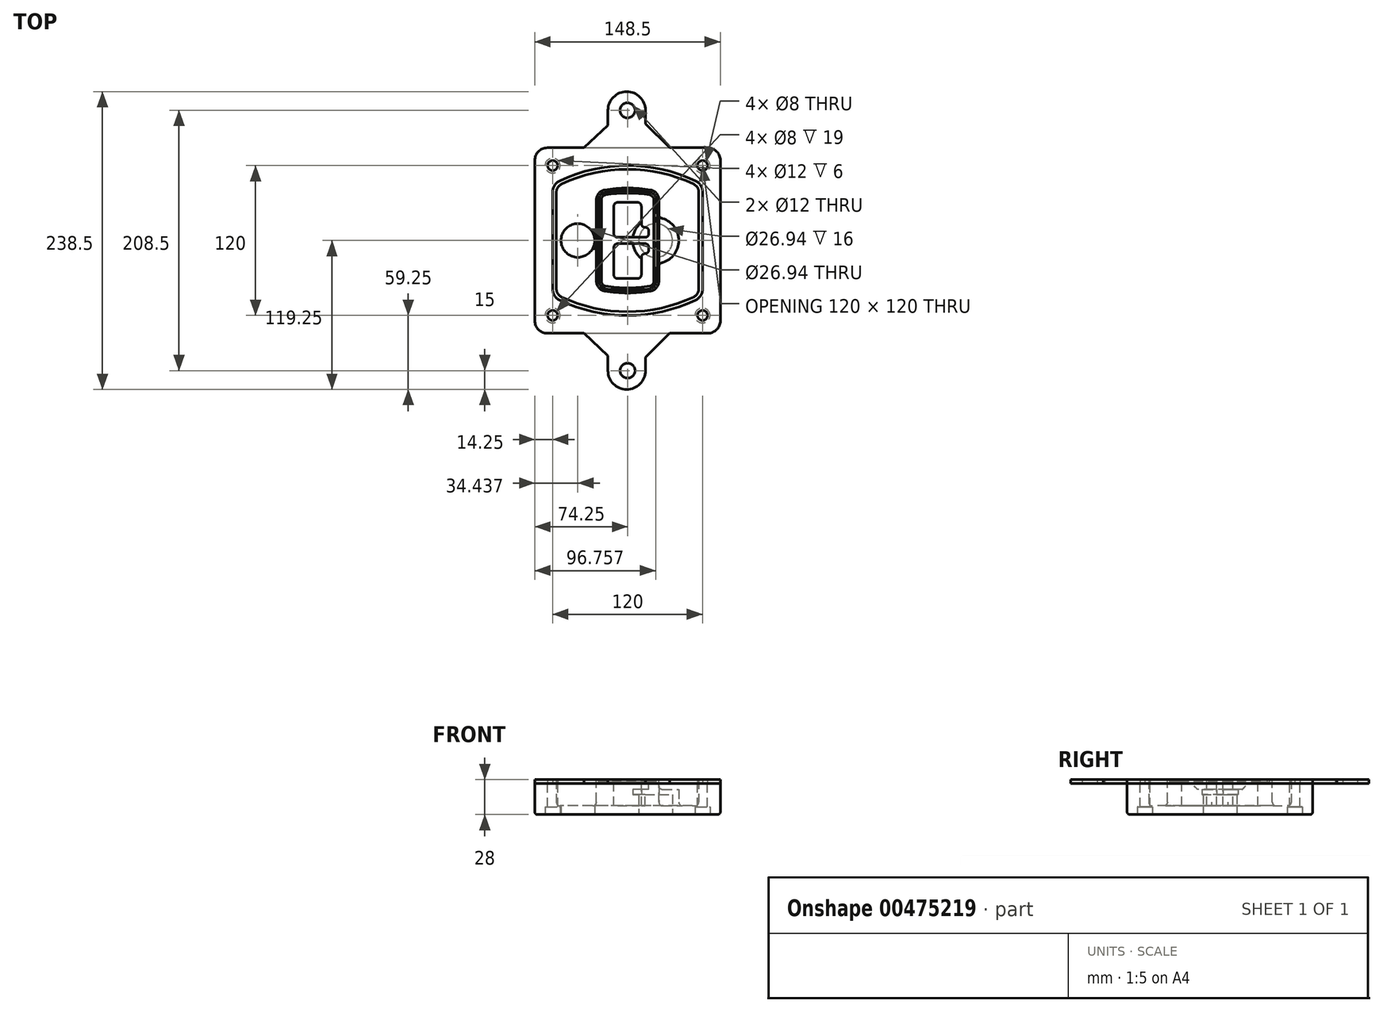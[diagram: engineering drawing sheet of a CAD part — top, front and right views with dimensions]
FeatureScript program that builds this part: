
annotation { "Feature Type Name" : "Feature", "Feature Type Description" : "" }
export const myFeature = defineFeature(function(context is Context, id is Id, definition is map)
    precondition{}
    {
        {
            var Q0;
            Q0=qCreatedBy(makeId("Top.planeOp"),FACE);
            var sketch = newSketch(context, id + "F0", { "sketchPlane" : qUnion([Q0])});
            skPoint(sketch, "E0.rect.middle", {"position": v(0, 0) * mm});
            skLineSegment(sketch, "E1.bottom", {"start": v(-64.25, -74.25) * mm, "end": v(64.25, -74.25) * mm});
            skLineSegment(sketch, "E1.top", {"start": v(-64.25, 74.25) * mm, "end": v(64.25, 74.25) * mm});
            skLineSegment(sketch, "E1.left", {"start": v(-74.25, -64.25) * mm, "end": v(-74.25, 64.25) * mm});
            skLineSegment(sketch, "E1.right", {"start": v(74.25, -64.25) * mm, "end": v(74.25, 64.25) * mm});
            skLineSegment(sketch, "E2", {"start": v(-74.25, 74.25) * mm, "end": v(74.25, -74.25) * mm, "construction": true});
            skLineSegment(sketch, "E3", {"start": v(74.25, 74.25) * mm, "end": v(-74.25, -74.25) * mm, "construction": true});
            skCircle(sketch, "E4", {"center": v(-60, 60) * mm, "radius": 4 * mm});
            skCircle(sketch, "E5", {"center": v(60, 60) * mm, "radius": 4 * mm});
            skCircle(sketch, "E6", {"center": v(60, -60) * mm, "radius": 4 * mm});
            skCircle(sketch, "E7", {"center": v(-60, -60) * mm, "radius": 4 * mm});
            skLineSegment(sketch, "E8", {"start": v(-60, 60) * mm, "end": v(60, 60) * mm, "construction": true});
            skLineSegment(sketch, "E9", {"start": v(60, 60) * mm, "end": v(60, -60) * mm, "construction": true});
            skLineSegment(sketch, "E10", {"start": v(60, -60) * mm, "end": v(-60, -60) * mm, "construction": true});
            skLineSegment(sketch, "E11", {"start": v(-60, -60) * mm, "end": v(-60, 60) * mm, "construction": true});
            skLineSegment(sketch, "E12", {"start": v(-60, 38.83) * mm, "end": v(-60, -38.83) * mm});
            skLineSegment(sketch, "E13", {"start": v(60, 38.83) * mm, "end": v(60, -38.83) * mm});
            skArc(sketch, "E14", {"start": v(54.26, 47.88) * mm, "mid": v(0, 60) * mm, "end": v(-54.26, 47.88) * mm});
            skArc(sketch, "E15", {"start": v(-54.26, -47.88) * mm, "mid": v(0, -60) * mm, "end": v(54.26, -47.88) * mm});
            skLineSegment(sketch, "E16", {"start": v(-60, 0) * mm, "end": v(60, 0) * mm, "construction": true});
            skPoint(sketch, "E17.visualSharp", {"position": v(-60, -45) * mm});
            skArc(sketch, "E17.filletArc", {"start": v(-60, -38.83) * mm, "mid": v(-58.44, -44.2) * mm, "end": v(-54.26, -47.88) * mm});
            skPoint(sketch, "E18.visualSharp", {"position": v(-60, 45) * mm});
            skArc(sketch, "E18.filletArc", {"start": v(-54.26, 47.88) * mm, "mid": v(-58.44, 44.2) * mm, "end": v(-60, 38.83) * mm});
            skPoint(sketch, "E19.visualSharp", {"position": v(60, 45) * mm});
            skArc(sketch, "E19.filletArc", {"start": v(60, 38.83) * mm, "mid": v(58.44, 44.2) * mm, "end": v(54.26, 47.88) * mm});
            skPoint(sketch, "E20.visualSharp", {"position": v(60, -45) * mm});
            skArc(sketch, "E20.filletArc", {"start": v(54.26, -47.88) * mm, "mid": v(58.44, -44.2) * mm, "end": v(60, -38.83) * mm});
            skPoint(sketch, "E21.visualSharp", {"position": v(-74.25, 74.25) * mm});
            skArc(sketch, "E21.filletArc", {"start": v(-64.25, 74.25) * mm, "mid": v(-71.32, 71.32) * mm, "end": v(-74.25, 64.25) * mm});
            skPoint(sketch, "E22.visualSharp", {"position": v(74.25, 74.25) * mm});
            skArc(sketch, "E22.filletArc", {"start": v(74.25, 64.25) * mm, "mid": v(71.32, 71.32) * mm, "end": v(64.25, 74.25) * mm});
            skPoint(sketch, "E23.visualSharp", {"position": v(74.25, -74.25) * mm});
            skArc(sketch, "E23.filletArc", {"start": v(64.25, -74.25) * mm, "mid": v(71.32, -71.32) * mm, "end": v(74.25, -64.25) * mm});
            skPoint(sketch, "E24.visualSharp", {"position": v(-74.25, -74.25) * mm});
            skArc(sketch, "E24.filletArc", {"start": v(-74.25, -64.25) * mm, "mid": v(-71.32, -71.32) * mm, "end": v(-64.25, -74.25) * mm});
            skArc(sketch, "E25.0", {"start": v(57, 38.83) * mm, "mid": v(55.9, 42.58) * mm, "end": v(52.98, 45.17) * mm});
            skLineSegment(sketch, "E25.1", {"start": v(57, 38.83) * mm, "end": v(57, -38.83) * mm});
            skArc(sketch, "E25.2", {"start": v(52.98, -45.17) * mm, "mid": v(55.9, -42.58) * mm, "end": v(57, -38.83) * mm});
            skArc(sketch, "E25.3", {"start": v(-52.98, -45.17) * mm, "mid": v(0, -57) * mm, "end": v(52.98, -45.17) * mm});
            skArc(sketch, "E25.4", {"start": v(-57, -38.83) * mm, "mid": v(-55.9, -42.58) * mm, "end": v(-52.98, -45.17) * mm});
            skArc(sketch, "E25.5", {"start": v(52.98, 45.17) * mm, "mid": v(0, 57) * mm, "end": v(-52.98, 45.17) * mm});
            skLineSegment(sketch, "E25.6", {"start": v(-57, 38.83) * mm, "end": v(-57, -38.83) * mm});
            skArc(sketch, "E25.7", {"start": v(-52.98, 45.17) * mm, "mid": v(-55.9, 42.58) * mm, "end": v(-57, 38.83) * mm});
            skArc(sketch, "E26.0", {"start": v(-55.96, 51.5) * mm, "mid": v(-61.82, 46.33) * mm, "end": v(-64, 38.83) * mm});
            skArc(sketch, "E26.1", {"start": v(55.96, 51.5) * mm, "mid": v(0, 64) * mm, "end": v(-55.96, 51.5) * mm});
            skArc(sketch, "E26.2", {"start": v(64, 38.83) * mm, "mid": v(61.82, 46.33) * mm, "end": v(55.96, 51.5) * mm});
            skLineSegment(sketch, "E26.3", {"start": v(64, 38.83) * mm, "end": v(64, -38.83) * mm});
            skArc(sketch, "E26.4", {"start": v(55.96, -51.5) * mm, "mid": v(61.82, -46.33) * mm, "end": v(64, -38.83) * mm});
            skLineSegment(sketch, "E26.5", {"start": v(-64, 38.83) * mm, "end": v(-64, -38.83) * mm});
            skArc(sketch, "E26.6", {"start": v(-55.96, -51.5) * mm, "mid": v(0, -64) * mm, "end": v(55.96, -51.5) * mm});
            skArc(sketch, "E26.7", {"start": v(-64, -38.83) * mm, "mid": v(-61.82, -46.33) * mm, "end": v(-55.96, -51.5) * mm});
            skSolve(sketch);
        }
        {
            var Q0;
            Q0=makeQuery(id+"F0.imprint","IMPRINT",FACE,{"disambiguationData":[TD([[makeQuery(id+"F0.imprint","IMPRINT",EDGE,{"derivedFrom":sQuery(id+"F0.wireOp",EDGE,"E1.bottom")}),1.0]])]});
            var Q1;
            Q1=makeQuery(id+"F0.imprint","IMPRINT",FACE,{"disambiguationData":[TD([[makeQuery(id+"F0.imprint","IMPRINT",EDGE,{"derivedFrom":sQuery(id+"F0.wireOp",EDGE,"E12")}),1.0]])]});
            var Q2;
            Q2=makeQuery(id+"F0.imprint","IMPRINT",FACE,{"disambiguationData":[TD([[makeQuery(id+"F0.imprint","IMPRINT",EDGE,{"derivedFrom":sQuery(id+"F0.wireOp",EDGE,"E25.0")}),1.0]])]});
            var Q3;
            Q3=makeQuery(id+"F0.imprint","IMPRINT",FACE,{"disambiguationData":[TD([[makeQuery(id+"F0.imprint","IMPRINT",EDGE,{"derivedFrom":sQuery(id+"F0.wireOp",EDGE,"E12")}),-1.0]])]});
            extrude(context, id + "F1", {"entities" : qUnion([Q0, Q1, Q2, Q3]), "oppositeDirection" : true, "depth" : 25 * mm});
        }
        {
            var Q0;
            Q0=makeQuery(id+"F0.imprint","IMPRINT",FACE,{"disambiguationData":[TD([[makeQuery(id+"F0.imprint","IMPRINT",EDGE,{"derivedFrom":sQuery(id+"F0.wireOp",EDGE,"E12")}),1.0]])]});
            extrude(context, id + "F2", {"entities" : qUnion([Q0]), "operationType" : NewBodyOperationType.ADD, "depth" : 3 * mm});
        }
        {
            var Q0;
            Q0=makeQuery(id+"F0.imprint","IMPRINT",FACE,{"disambiguationData":[TD([[makeQuery(id+"F0.imprint","IMPRINT",EDGE,{"derivedFrom":sQuery(id+"F0.wireOp",EDGE,"E25.0")}),1.0]])]});
            extrude(context, id + "F3", {"entities" : qUnion([Q0]), "operationType" : NewBodyOperationType.REMOVE, "oppositeDirection" : true, "depth" : 18 * mm});
        }
        {
            var Q0;
            Q0=makeQuery(id+"F2.opExtrude","CAP_FACE",FACE,{"disambiguationData":[OSD([sQuery(id+"F0.wireOp",EDGE,"E12"),sQuery(id+"F0.wireOp",EDGE,"E13"),sQuery(id+"F0.wireOp",EDGE,"E14"),sQuery(id+"F0.wireOp",EDGE,"E15"),sQuery(id+"F0.wireOp",EDGE,"E17.filletArc"),sQuery(id+"F0.wireOp",EDGE,"E18.filletArc"),sQuery(id+"F0.wireOp",EDGE,"E19.filletArc"),sQuery(id+"F0.wireOp",EDGE,"E20.filletArc"),sQuery(id+"F0.wireOp",EDGE,"E25.0"),sQuery(id+"F0.wireOp",EDGE,"E25.1"),sQuery(id+"F0.wireOp",EDGE,"E25.2"),sQuery(id+"F0.wireOp",EDGE,"E25.3"),sQuery(id+"F0.wireOp",EDGE,"E25.4"),sQuery(id+"F0.wireOp",EDGE,"E25.5"),sQuery(id+"F0.wireOp",EDGE,"E25.6"),sQuery(id+"F0.wireOp",EDGE,"E25.7")])],"isStart":false});
            var sketch = newSketch(context, id + "F4", { "sketchPlane" : qUnion([Q0])});
            skArc(sketch, "E27.0", {"start": v(-18.34, -40.45) * mm, "mid": v(0, -42) * mm, "end": v(18.34, -40.45) * mm});
            skArc(sketch, "E28.0", {"start": v(18.34, 40.45) * mm, "mid": v(0, 42) * mm, "end": v(-18.34, 40.45) * mm});
            skLineSegment(sketch, "E29", {"start": v(-25, 32.57) * mm, "end": v(-25, -32.57) * mm});
            skLineSegment(sketch, "E30", {"start": v(25, 32.57) * mm, "end": v(25, -32.57) * mm});
            skLineSegment(sketch, "E31", {"start": v(-25, 39.1) * mm, "end": v(25, 39.1) * mm, "construction": true});
            skLineSegment(sketch, "E32", {"start": v(-25, -39.1) * mm, "end": v(25, -39.1) * mm, "construction": true});
            skPoint(sketch, "E33.visualSharp", {"position": v(-25, 39.1) * mm});
            skArc(sketch, "E33.filletArc", {"start": v(-18.34, 40.45) * mm, "mid": v(-23.11, 37.73) * mm, "end": v(-25, 32.57) * mm});
            skPoint(sketch, "E34.visualSharp", {"position": v(25, 39.1) * mm});
            skArc(sketch, "E34.filletArc", {"start": v(25, 32.57) * mm, "mid": v(23.11, 37.73) * mm, "end": v(18.34, 40.45) * mm});
            skPoint(sketch, "E35.visualSharp", {"position": v(25, -39.1) * mm});
            skArc(sketch, "E35.filletArc", {"start": v(18.34, -40.45) * mm, "mid": v(23.11, -37.73) * mm, "end": v(25, -32.57) * mm});
            skPoint(sketch, "E36.visualSharp", {"position": v(-25, -39.1) * mm});
            skArc(sketch, "E36.filletArc", {"start": v(-25, -32.57) * mm, "mid": v(-23.11, -37.73) * mm, "end": v(-18.34, -40.45) * mm});
            skArc(sketch, "E37.0", {"start": v(52.98, 45.17) * mm, "mid": v(0, 57) * mm, "end": v(-52.98, 45.17) * mm});
            skArc(sketch, "E37.1", {"start": v(-52.98, 45.17) * mm, "mid": v(-55.9, 42.58) * mm, "end": v(-57, 38.83) * mm});
            skLineSegment(sketch, "E37.2", {"start": v(-57, 38.83) * mm, "end": v(-57, -38.83) * mm});
            skArc(sketch, "E37.3", {"start": v(-57, -38.83) * mm, "mid": v(-55.9, -42.58) * mm, "end": v(-52.98, -45.17) * mm});
            skArc(sketch, "E37.4", {"start": v(-52.98, -45.17) * mm, "mid": v(0, -57) * mm, "end": v(52.98, -45.17) * mm});
            skArc(sketch, "E37.5", {"start": v(52.98, -45.17) * mm, "mid": v(55.9, -42.58) * mm, "end": v(57, -38.83) * mm});
            skLineSegment(sketch, "E37.6", {"start": v(57, 38.83) * mm, "end": v(57, -38.83) * mm});
            skArc(sketch, "E37.7", {"start": v(57, 38.83) * mm, "mid": v(55.9, 42.58) * mm, "end": v(52.98, 45.17) * mm});
            skLineSegment(sketch, "E38.0", {"start": v(23, 32.57) * mm, "end": v(23, -32.57) * mm});
            skArc(sketch, "E38.1", {"start": v(18, -38.48) * mm, "mid": v(21.58, -36.44) * mm, "end": v(23, -32.57) * mm});
            skArc(sketch, "E38.2", {"start": v(-18, -38.48) * mm, "mid": v(0, -40) * mm, "end": v(18, -38.48) * mm});
            skArc(sketch, "E38.3", {"start": v(-23, -32.57) * mm, "mid": v(-21.58, -36.44) * mm, "end": v(-18, -38.48) * mm});
            skLineSegment(sketch, "E38.4", {"start": v(-23, 32.57) * mm, "end": v(-23, -32.57) * mm});
            skArc(sketch, "E38.5", {"start": v(23, 32.57) * mm, "mid": v(21.58, 36.44) * mm, "end": v(18, 38.48) * mm});
            skArc(sketch, "E38.6", {"start": v(-18, 38.48) * mm, "mid": v(-21.58, 36.44) * mm, "end": v(-23, 32.57) * mm});
            skArc(sketch, "E38.7", {"start": v(18, 38.48) * mm, "mid": v(0, 40) * mm, "end": v(-18, 38.48) * mm});
            skArc(sketch, "E39.0", {"start": v(21, 32.57) * mm, "mid": v(20.06, 35.15) * mm, "end": v(17.67, 36.5) * mm});
            skLineSegment(sketch, "E39.1", {"start": v(21, 32.57) * mm, "end": v(21, -32.57) * mm});
            skArc(sketch, "E39.2", {"start": v(17.67, -36.5) * mm, "mid": v(20.06, -35.15) * mm, "end": v(21, -32.57) * mm});
            skArc(sketch, "E39.3", {"start": v(-17.67, -36.5) * mm, "mid": v(0, -38) * mm, "end": v(17.67, -36.5) * mm});
            skArc(sketch, "E39.4", {"start": v(-21, -32.57) * mm, "mid": v(-20.06, -35.15) * mm, "end": v(-17.67, -36.5) * mm});
            skArc(sketch, "E39.5", {"start": v(17.67, 36.5) * mm, "mid": v(0, 38) * mm, "end": v(-17.67, 36.5) * mm});
            skLineSegment(sketch, "E39.6", {"start": v(-21, 32.57) * mm, "end": v(-21, -32.57) * mm});
            skArc(sketch, "E39.7", {"start": v(-17.67, 36.5) * mm, "mid": v(-20.06, 35.15) * mm, "end": v(-21, 32.57) * mm});
            skLineSegment(sketch, "E40", {"start": v(-25, 0) * mm, "end": v(25, 0) * mm, "construction": true});
            skLineSegment(sketch, "E41", {"start": v(-11, 5.5) * mm, "end": v(-11, 27.5) * mm});
            skLineSegment(sketch, "E42", {"start": v(-8, 30.5) * mm, "end": v(8, 30.5) * mm});
            skLineSegment(sketch, "E43", {"start": v(11, 27.5) * mm, "end": v(11, 13.5) * mm});
            skLineSegment(sketch, "E44", {"start": v(14, 10.5) * mm, "end": v(14, 10.5) * mm});
            skLineSegment(sketch, "E45", {"start": v(17, 7.5) * mm, "end": v(17, 5.5) * mm});
            skLineSegment(sketch, "E46", {"start": v(14, 2.5) * mm, "end": v(-8, 2.5) * mm});
            skPoint(sketch, "E47.visualSharp", {"position": v(-11, 30.5) * mm});
            skArc(sketch, "E47.filletArc", {"start": v(-8, 30.5) * mm, "mid": v(-10.12, 29.62) * mm, "end": v(-11, 27.5) * mm});
            skPoint(sketch, "E48.visualSharp", {"position": v(11, 30.5) * mm});
            skArc(sketch, "E48.filletArc", {"start": v(11, 27.5) * mm, "mid": v(10.12, 29.62) * mm, "end": v(8, 30.5) * mm});
            skPoint(sketch, "E49.visualSharp", {"position": v(11, 10.5) * mm});
            skArc(sketch, "E49.filletArc", {"start": v(11, 13.5) * mm, "mid": v(11.88, 11.38) * mm, "end": v(14, 10.5) * mm});
            skPoint(sketch, "E50.visualSharp", {"position": v(17, 10.5) * mm});
            skArc(sketch, "E50.filletArc", {"start": v(17, 7.5) * mm, "mid": v(16.12, 9.62) * mm, "end": v(14, 10.5) * mm});
            skPoint(sketch, "E51.visualSharp", {"position": v(17, 2.5) * mm});
            skArc(sketch, "E51.filletArc", {"start": v(14, 2.5) * mm, "mid": v(16.12, 3.38) * mm, "end": v(17, 5.5) * mm});
            skPoint(sketch, "E52.visualSharp", {"position": v(-11, 2.5) * mm});
            skArc(sketch, "E52.filletArc", {"start": v(-11, 5.5) * mm, "mid": v(-10.12, 3.38) * mm, "end": v(-8, 2.5) * mm});
            skLineSegment(sketch, "E53.0.MirrorCS", {"start": v(14, -2.5) * mm, "end": v(-8, -2.5) * mm});
            skArc(sketch, "E54.0.MirrorCS", {"start": v(-11, -5.5) * mm, "mid": v(-10.12, -3.38) * mm, "end": v(-8, -2.5) * mm});
            skLineSegment(sketch, "E55.0.MirrorCS", {"start": v(-11, -5.5) * mm, "end": v(-11, -27.5) * mm});
            skArc(sketch, "E56.0.MirrorCS", {"start": v(-8, -30.5) * mm, "mid": v(-10.12, -29.62) * mm, "end": v(-11, -27.5) * mm});
            skLineSegment(sketch, "E57.0.MirrorCS", {"start": v(-8, -30.5) * mm, "end": v(8, -30.5) * mm});
            skArc(sketch, "E58.0.MirrorCS", {"start": v(11, -27.5) * mm, "mid": v(10.12, -29.62) * mm, "end": v(8, -30.5) * mm});
            skLineSegment(sketch, "E59.0.MirrorCS", {"start": v(11, -27.5) * mm, "end": v(11, -13.5) * mm});
            skArc(sketch, "E60.0.MirrorCS", {"start": v(11, -13.5) * mm, "mid": v(11.88, -11.38) * mm, "end": v(14, -10.5) * mm});
            skArc(sketch, "E61.0.MirrorCS", {"start": v(17, -7.5) * mm, "mid": v(16.12, -9.62) * mm, "end": v(14, -10.5) * mm});
            skLineSegment(sketch, "E62.0.MirrorCS", {"start": v(17, -7.5) * mm, "end": v(17, -5.5) * mm});
            skArc(sketch, "E63.0.MirrorCS", {"start": v(14, -2.5) * mm, "mid": v(16.12, -3.38) * mm, "end": v(17, -5.5) * mm});
            skSolve(sketch);
        }
        {
            var Q0;
            Q0=makeQuery(id+"F4.imprint","IMPRINT",FACE,{"disambiguationData":[TD([[makeQuery(id+"F4.imprint","IMPRINT",EDGE,{"derivedFrom":sQuery(id+"F4.wireOp",EDGE,"E27.0")}),1.0]])]});
            var Q1;
            Q1=makeQuery(id+"F4.imprint","IMPRINT",FACE,{"disambiguationData":[TD([[makeQuery(id+"F4.imprint","IMPRINT",EDGE,{"derivedFrom":sQuery(id+"F4.wireOp",EDGE,"E38.0")}),-1.0]])]});
            var Q2;
            Q2=makeQuery(id+"F4.imprint","IMPRINT",FACE,{"disambiguationData":[TD([[makeQuery(id+"F4.imprint","IMPRINT",EDGE,{"derivedFrom":sQuery(id+"F4.wireOp",EDGE,"E39.0")}),1.0]])]});
            extrude(context, id + "F5", {"entities" : qUnion([Q0, Q1, Q2]), "operationType" : NewBodyOperationType.ADD, "endBound" : BoundingType.UP_TO_NEXT, "oppositeDirection" : true, "depth" : 25 * mm});
        }
        {
            var Q0;
            Q0=makeQuery(id+"F4.imprint","IMPRINT",FACE,{"disambiguationData":[TD([[makeQuery(id+"F4.imprint","IMPRINT",EDGE,{"derivedFrom":sQuery(id+"F4.wireOp",EDGE,"E38.0")}),-1.0]])]});
            extrude(context, id + "F6", {"entities" : qUnion([Q0]), "operationType" : NewBodyOperationType.REMOVE, "oppositeDirection" : true, "depth" : 2 * mm});
        }
        {
            var Q0;
            Q0=makeQuery(id+"F1.opExtrude","CAP_FACE",FACE,{"disambiguationData":[OSD([sQuery(id+"F0.wireOp",EDGE,"E1.bottom"),sQuery(id+"F0.wireOp",EDGE,"E1.top"),sQuery(id+"F0.wireOp",EDGE,"E1.left"),sQuery(id+"F0.wireOp",EDGE,"E1.right"),sQuery(id+"F0.wireOp",EDGE,"E4"),sQuery(id+"F0.wireOp",EDGE,"E5"),sQuery(id+"F0.wireOp",EDGE,"E6"),sQuery(id+"F0.wireOp",EDGE,"E7"),sQuery(id+"F0.wireOp",EDGE,"E21.filletArc"),sQuery(id+"F0.wireOp",EDGE,"E22.filletArc"),sQuery(id+"F0.wireOp",EDGE,"E23.filletArc"),sQuery(id+"F0.wireOp",EDGE,"E24.filletArc")])],"isStart":false});
            var sketch = newSketch(context, id + "F7", { "sketchPlane" : qUnion([Q0])});
            skCircle(sketch, "E64", {"center": v(22.5, 0) * mm, "radius": 13.47 * mm});
            skCircle(sketch, "E65", {"center": v(-39.81, 0) * mm, "radius": 13.47 * mm});
            skLineSegment(sketch, "E66", {"start": v(74.25, 0) * mm, "end": v(-74.25, 0) * mm});
            skCircle(sketch, "E67", {"center": v(22.5, 0) * mm, "radius": 18.47 * mm});
            skCircle(sketch, "E68", {"center": v(60, -60) * mm, "radius": 6 * mm});
            skCircle(sketch, "E69", {"center": v(-60, -60) * mm, "radius": 6 * mm});
            skCircle(sketch, "E70", {"center": v(-60, 60) * mm, "radius": 6 * mm});
            skCircle(sketch, "E71", {"center": v(60, 60) * mm, "radius": 6 * mm});
            skSolve(sketch);
        }
        {
            var Q0;
            {var subQ1=sQuery(id+"F7.wireOp",EDGE,"E66");var subQ4=sQuery(id+"F7.wireOp",EDGE,"E64");var subQ6=makeQuery(id+"F7.imprint","INTERSECT",VERTEX,{"disambiguationData":[OD(0.0)],"derivedFrom":[subQ4,subQ1]});Q0=makeQuery(id+"F7.imprint","IMPRINT",FACE,{"disambiguationData":[TD([[makeQuery(id+"F7.imprint","IMPRINT",EDGE,{"disambiguationData":[TD([[subQ6,-1.0]])],"derivedFrom":subQ4}),-1.0]])]});}
            var Q1;
            {var subQ0=sQuery(id+"F7.wireOp",EDGE,"E66");var subQ1=sQuery(id+"F7.wireOp",EDGE,"E64");var subQ3=makeQuery(id+"F7.imprint","INTERSECT",VERTEX,{"disambiguationData":[OD(0.0)],"derivedFrom":[subQ1,subQ0]});Q1=makeQuery(id+"F7.imprint","IMPRINT",FACE,{"disambiguationData":[TD([[makeQuery(id+"F7.imprint","IMPRINT",EDGE,{"disambiguationData":[TD([[subQ3,-1.0]])],"derivedFrom":subQ1}),1.0]])]});}
            var Q2;
            {var subQ0=sQuery(id+"F7.wireOp",EDGE,"E66");var subQ1=sQuery(id+"F7.wireOp",EDGE,"E64");var subQ3=makeQuery(id+"F7.imprint","INTERSECT",VERTEX,{"disambiguationData":[OD(0.0)],"derivedFrom":[subQ1,subQ0]});Q2=makeQuery(id+"F7.imprint","IMPRINT",FACE,{"disambiguationData":[TD([[makeQuery(id+"F7.imprint","IMPRINT",EDGE,{"disambiguationData":[TD([[subQ3,1.0]])],"derivedFrom":subQ1}),1.0]])]});}
            var Q3;
            {var subQ1=sQuery(id+"F7.wireOp",EDGE,"E66");var subQ4=sQuery(id+"F7.wireOp",EDGE,"E64");var subQ6=makeQuery(id+"F7.imprint","INTERSECT",VERTEX,{"disambiguationData":[OD(0.0)],"derivedFrom":[subQ4,subQ1]});Q3=makeQuery(id+"F7.imprint","IMPRINT",FACE,{"disambiguationData":[TD([[makeQuery(id+"F7.imprint","IMPRINT",EDGE,{"disambiguationData":[TD([[subQ6,1.0]])],"derivedFrom":subQ4}),-1.0]])]});}
            extrude(context, id + "F8", {"entities" : qUnion([Q0, Q1, Q2, Q3]), "operationType" : NewBodyOperationType.ADD, "oppositeDirection" : true, "depth" : 20 * mm});
        }
        {
            var Q0;
            {var subQ0=sQuery(id+"F7.wireOp",EDGE,"E66");var subQ1=sQuery(id+"F7.wireOp",EDGE,"E64");var subQ3=makeQuery(id+"F7.imprint","INTERSECT",VERTEX,{"disambiguationData":[OD(0.0)],"derivedFrom":[subQ1,subQ0]});Q0=makeQuery(id+"F7.imprint","IMPRINT",FACE,{"disambiguationData":[TD([[makeQuery(id+"F7.imprint","IMPRINT",EDGE,{"disambiguationData":[TD([[subQ3,-1.0]])],"derivedFrom":subQ1}),1.0]])]});}
            var Q1;
            {var subQ0=sQuery(id+"F7.wireOp",EDGE,"E66");var subQ1=sQuery(id+"F7.wireOp",EDGE,"E64");var subQ3=makeQuery(id+"F7.imprint","INTERSECT",VERTEX,{"disambiguationData":[OD(0.0)],"derivedFrom":[subQ1,subQ0]});Q1=makeQuery(id+"F7.imprint","IMPRINT",FACE,{"disambiguationData":[TD([[makeQuery(id+"F7.imprint","IMPRINT",EDGE,{"disambiguationData":[TD([[subQ3,1.0]])],"derivedFrom":subQ1}),1.0]])]});}
            extrude(context, id + "F9", {"entities" : qUnion([Q0, Q1]), "operationType" : NewBodyOperationType.REMOVE, "oppositeDirection" : true, "depth" : 16 * mm});
        }
        {
            var Q0;
            {var subQ0=sQuery(id+"F7.wireOp",EDGE,"E66");var subQ1=sQuery(id+"F7.wireOp",EDGE,"E65");var subQ3=makeQuery(id+"F7.imprint","INTERSECT",VERTEX,{"disambiguationData":[OD(0.0)],"derivedFrom":[subQ1,subQ0]});Q0=makeQuery(id+"F7.imprint","IMPRINT",FACE,{"disambiguationData":[TD([[makeQuery(id+"F7.imprint","IMPRINT",EDGE,{"disambiguationData":[TD([[subQ3,-1.0]])],"derivedFrom":subQ1}),1.0]])]});}
            var Q1;
            {var subQ0=sQuery(id+"F7.wireOp",EDGE,"E66");var subQ1=sQuery(id+"F7.wireOp",EDGE,"E65");var subQ3=makeQuery(id+"F7.imprint","INTERSECT",VERTEX,{"disambiguationData":[OD(0.0)],"derivedFrom":[subQ1,subQ0]});Q1=makeQuery(id+"F7.imprint","IMPRINT",FACE,{"disambiguationData":[TD([[makeQuery(id+"F7.imprint","IMPRINT",EDGE,{"disambiguationData":[TD([[subQ3,1.0]])],"derivedFrom":subQ1}),1.0]])]});}
            extrude(context, id + "F10", {"entities" : qUnion([Q0, Q1]), "operationType" : NewBodyOperationType.REMOVE, "oppositeDirection" : true, "depth" : 25 * mm});
        }
        {
            var Q0;
            Q0=makeQuery(id+"F7.imprint","IMPRINT",FACE,{"disambiguationData":[TD([[makeQuery(id+"F7.imprint","IMPRINT",EDGE,{"derivedFrom":sQuery(id+"F7.wireOp",EDGE,"E68")}),1.0]])]});
            var Q1;
            Q1=makeQuery(id+"F7.imprint","IMPRINT",FACE,{"disambiguationData":[TD([[makeQuery(id+"F7.imprint","IMPRINT",EDGE,{"derivedFrom":makeQuery(id+"F1.opExtrude","CAP_EDGE",EDGE,{"disambiguationData":[OSD([sQuery(id+"F0.wireOp",EDGE,"E5")])],"isStart":false})}),-1.0]])]});
            var Q2;
            Q2=makeQuery(id+"F7.imprint","IMPRINT",FACE,{"disambiguationData":[TD([[makeQuery(id+"F7.imprint","IMPRINT",EDGE,{"derivedFrom":sQuery(id+"F7.wireOp",EDGE,"E69")}),1.0]])]});
            var Q3;
            Q3=makeQuery(id+"F7.imprint","IMPRINT",FACE,{"disambiguationData":[TD([[makeQuery(id+"F7.imprint","IMPRINT",EDGE,{"derivedFrom":makeQuery(id+"F1.opExtrude","CAP_EDGE",EDGE,{"disambiguationData":[OSD([sQuery(id+"F0.wireOp",EDGE,"E4")])],"isStart":false})}),-1.0]])]});
            var Q4;
            Q4=makeQuery(id+"F7.imprint","IMPRINT",FACE,{"disambiguationData":[TD([[makeQuery(id+"F7.imprint","IMPRINT",EDGE,{"derivedFrom":sQuery(id+"F7.wireOp",EDGE,"E70")}),1.0]])]});
            var Q5;
            Q5=makeQuery(id+"F7.imprint","IMPRINT",FACE,{"disambiguationData":[TD([[makeQuery(id+"F7.imprint","IMPRINT",EDGE,{"derivedFrom":makeQuery(id+"F1.opExtrude","CAP_EDGE",EDGE,{"disambiguationData":[OSD([sQuery(id+"F0.wireOp",EDGE,"E7")])],"isStart":false})}),-1.0]])]});
            var Q6;
            Q6=makeQuery(id+"F7.imprint","IMPRINT",FACE,{"disambiguationData":[TD([[makeQuery(id+"F7.imprint","IMPRINT",EDGE,{"derivedFrom":sQuery(id+"F7.wireOp",EDGE,"E71")}),1.0]])]});
            var Q7;
            Q7=makeQuery(id+"F7.imprint","IMPRINT",FACE,{"disambiguationData":[TD([[makeQuery(id+"F7.imprint","IMPRINT",EDGE,{"derivedFrom":makeQuery(id+"F1.opExtrude","CAP_EDGE",EDGE,{"disambiguationData":[OSD([sQuery(id+"F0.wireOp",EDGE,"E6")])],"isStart":false})}),-1.0]])]});
            extrude(context, id + "F11", {"entities" : qUnion([Q0, Q1, Q2, Q3, Q4, Q5, Q6, Q7]), "operationType" : NewBodyOperationType.REMOVE, "oppositeDirection" : true, "depth" : 6 * mm});
        }
        {
            var Q0;
            Q0=makeQuery(id+"F9.boolean.opBoolean","COPY",FACE,{"derivedFrom":makeQuery(id+"F9.opExtrude","CAP_FACE",FACE,{"disambiguationData":[OSD([sQuery(id+"F7.wireOp",EDGE,"E64")])],"isStart":false})});
            var sketch = newSketch(context, id + "F12", { "sketchPlane" : qUnion([Q0])});
            skArc(sketch, "E72.0", {"start": v(11, 14.45) * mm, "mid": v(6.45, 9.13) * mm, "end": v(4.2, 2.5) * mm});
            skArc(sketch, "E72.1", {"start": v(4.2, -2.5) * mm, "mid": v(6.45, -9.13) * mm, "end": v(11, -14.45) * mm});
            skLineSegment(sketch, "E73", {"start": v(4.2, -2.5) * mm, "end": v(14, -2.5) * mm});
            skLineSegment(sketch, "E74.0", {"start": v(14, 2.5) * mm, "end": v(4.2, 2.5) * mm});
            skArc(sketch, "E74.1", {"start": v(14, 2.5) * mm, "mid": v(16.12, 3.38) * mm, "end": v(17, 5.5) * mm});
            skLineSegment(sketch, "E74.2", {"start": v(17, 7.5) * mm, "end": v(17, 5.5) * mm});
            skArc(sketch, "E74.3", {"start": v(17, 7.5) * mm, "mid": v(16.12, 9.62) * mm, "end": v(14, 10.5) * mm});
            skArc(sketch, "E74.4", {"start": v(11, 13.5) * mm, "mid": v(11.88, 11.38) * mm, "end": v(14, 10.5) * mm});
            skLineSegment(sketch, "E74.5", {"start": v(11, 14.45) * mm, "end": v(11, 13.5) * mm});
            skLineSegment(sketch, "E74.7", {"start": v(14, -2.5) * mm, "end": v(4.2, -2.5) * mm});
            skArc(sketch, "E74.8", {"start": v(14, -2.5) * mm, "mid": v(16.12, -3.38) * mm, "end": v(17, -5.5) * mm});
            skLineSegment(sketch, "E74.9", {"start": v(17, -7.5) * mm, "end": v(17, -5.5) * mm});
            skArc(sketch, "E74.10", {"start": v(17, -7.5) * mm, "mid": v(16.12, -9.62) * mm, "end": v(14, -10.5) * mm});
            skArc(sketch, "E74.11", {"start": v(11, -13.5) * mm, "mid": v(11.88, -11.38) * mm, "end": v(14, -10.5) * mm});
            skLineSegment(sketch, "E74.12", {"start": v(11, -14.45) * mm, "end": v(11, -13.5) * mm});
            skPoint(sketch, "E75.orphan", {"position": v(11, -27.5) * mm});
            skPoint(sketch, "E76.orphan", {"position": v(-8, -2.5) * mm});
            skPoint(sketch, "E77.orphan", {"position": v(-8, 2.5) * mm});
            skPoint(sketch, "E78.orphan", {"position": v(11, 27.5) * mm});
            skSolve(sketch);
        }
        {
            var Q0;
            {var subQ7=sQuery(id+"F12.wireOp",EDGE,"E72.0");var subQ14=sQuery(id+"F12.wireOp",EDGE,"E72.1");var subQ16=sQuery(id+"F12.wireOp",EDGE,"E74.1");var subQ18=sQuery(id+"F12.wireOp",EDGE,"E74.8");Q0=qUnion([makeQuery(id+"F12.imprint","IMPRINT",FACE,{"disambiguationData":[TD([[makeQuery(id+"F12.imprint","IMPRINT",EDGE,{"derivedFrom":subQ7}),1.0]])]}),makeQuery(id+"F12.imprint","IMPRINT",FACE,{"disambiguationData":[TD([[makeQuery(id+"F12.imprint","IMPRINT",EDGE,{"derivedFrom":subQ14}),1.0]])]}),makeQuery(id+"F12.imprint","IMPRINT",FACE,{"disambiguationData":[TD([[makeQuery(id+"F12.imprint","IMPRINT",EDGE,{"derivedFrom":subQ16}),1.0]])]}),makeQuery(id+"F12.imprint","IMPRINT",FACE,{"disambiguationData":[TD([[makeQuery(id+"F12.imprint","IMPRINT",EDGE,{"derivedFrom":subQ18}),-1.0]])]})]);}
            var Q1;
            Q1=makeQuery(id+"F5.boolean.opBoolean","SPLIT",FACE,{"disambiguationData":[TD([makeQuery(id+"F5.opExtrude","SWEPT_FACE",FACE,{"disambiguationData":[OSD([sQuery(id+"F4.wireOp",EDGE,"E41")])]})])],"derivedFrom":makeQuery(id+"F3.boolean.opBoolean","COPY",FACE,{"derivedFrom":makeQuery(id+"F3.opExtrude","CAP_FACE",FACE,{"disambiguationData":[OSD([sQuery(id+"F0.wireOp",EDGE,"E25.0"),sQuery(id+"F0.wireOp",EDGE,"E25.1"),sQuery(id+"F0.wireOp",EDGE,"E25.2"),sQuery(id+"F0.wireOp",EDGE,"E25.3"),sQuery(id+"F0.wireOp",EDGE,"E25.4"),sQuery(id+"F0.wireOp",EDGE,"E25.5"),sQuery(id+"F0.wireOp",EDGE,"E25.6"),sQuery(id+"F0.wireOp",EDGE,"E25.7")])],"isStart":false})})});
            extrude(context, id + "F13", {"entities" : qUnion([Q0]), "operationType" : NewBodyOperationType.REMOVE, "endBound" : BoundingType.UP_TO_SURFACE, "endBoundEntityFace" : qUnion([Q1]), "depth" : 25 * mm});
        }
        {
            var Q0;
            Q0=makeQuery(id+"F3.boolean.opBoolean","COPY",EDGE,{"derivedFrom":makeQuery(id+"F3.opExtrude","CAP_EDGE",EDGE,{"disambiguationData":[OSD([sQuery(id+"F0.wireOp",EDGE,"E25.6")])],"isStart":false})});
            var Q1;
            Q1=makeQuery(id+"F8.boolean.opBoolean","INTERSECT",EDGE,{"derivedFrom":[makeQuery(id+"F5.opExtrude","SWEPT_FACE",FACE,{"disambiguationData":[OSD([sQuery(id+"F4.wireOp",EDGE,"E30")])]}),makeQuery(id+"F8.opExtrude","CAP_FACE",FACE,{"disambiguationData":[OSD([sQuery(id+"F7.wireOp",EDGE,"E67")])],"isStart":false})]});
            var Q2;
            Q2=makeQuery(id+"F8.boolean.opBoolean","INTERSECT",EDGE,{"disambiguationData":[OD(1.0)],"derivedFrom":[makeQuery(id+"F5.opExtrude","SWEPT_FACE",FACE,{"disambiguationData":[OSD([sQuery(id+"F4.wireOp",EDGE,"E30")])]}),makeQuery(id+"F8.opExtrude","SWEPT_FACE",FACE,{"disambiguationData":[OSD([sQuery(id+"F7.wireOp",EDGE,"E67")])]})]});
            var Q3;
            {var subQ0=sQuery(id+"F4.wireOp",EDGE,"E30");Q3=makeQuery(id+"F8.boolean.opBoolean","SPLIT",EDGE,{"disambiguationData":[TD([makeQuery(id+"F5.opExtrude","SWEPT_FACE",FACE,{"disambiguationData":[OSD([sQuery(id+"F4.wireOp",EDGE,"E35.filletArc")])]})])],"derivedFrom":makeQuery(id+"F5.opExtrude","CAP_EDGE",EDGE,{"disambiguationData":[OSD([subQ0])],"isStart":false})});}
            var Q4;
            {var subQ0=sQuery(id+"F0.wireOp",EDGE,"E25.7");var subQ1=sQuery(id+"F0.wireOp",EDGE,"E25.1");var subQ2=sQuery(id+"F0.wireOp",EDGE,"E25.6");var subQ3=sQuery(id+"F0.wireOp",EDGE,"E25.5");var subQ4=sQuery(id+"F0.wireOp",EDGE,"E25.4");var subQ5=sQuery(id+"F0.wireOp",EDGE,"E25.0");var subQ6=sQuery(id+"F0.wireOp",EDGE,"E25.2");var subQ7=sQuery(id+"F0.wireOp",EDGE,"E25.3");Q4=makeQuery(id+"F8.boolean.opBoolean","INTERSECT",EDGE,{"derivedFrom":[makeQuery(id+"F5.boolean.opBoolean","SPLIT",FACE,{"disambiguationData":[TD([makeQuery(id+"F2.opExtrude","SWEPT_FACE",FACE,{"disambiguationData":[OSD([subQ5])]})])],"derivedFrom":makeQuery(id+"F3.boolean.opBoolean","COPY",FACE,{"derivedFrom":makeQuery(id+"F3.opExtrude","CAP_FACE",FACE,{"disambiguationData":[OSD([subQ5,subQ1,subQ6,subQ7,subQ4,subQ3,subQ2,subQ0])],"isStart":false})})}),makeQuery(id+"F8.opExtrude","SWEPT_FACE",FACE,{"disambiguationData":[OSD([sQuery(id+"F7.wireOp",EDGE,"E67")])]})]});}
            var Q5;
            Q5=makeQuery(id+"F8.boolean.opBoolean","INTERSECT",EDGE,{"disambiguationData":[OD(0.0)],"derivedFrom":[makeQuery(id+"F5.opExtrude","SWEPT_FACE",FACE,{"disambiguationData":[OSD([sQuery(id+"F4.wireOp",EDGE,"E30")])]}),makeQuery(id+"F8.opExtrude","SWEPT_FACE",FACE,{"disambiguationData":[OSD([sQuery(id+"F7.wireOp",EDGE,"E67")])]})]});
            fillet(context, id + "F14", {"entities" : qUnion([Q0, Q1, Q2, Q3, Q4, Q5]), "radius" : 3 * mm, "tangentPropagation" : true, "allowEdgeOverflow" : false});
        }
        {
            var Q0;
            Q0=makeQuery(id+"F1.opExtrude","CAP_EDGE",EDGE,{"disambiguationData":[OSD([sQuery(id+"F0.wireOp",EDGE,"E1.bottom")])],"isStart":false});
            fillet(context, id + "F15", {"entities" : qUnion([Q0]), "radius" : 2 * mm, "tangentPropagation" : true, "allowEdgeOverflow" : false});
        }
        {
            var Q0;
            {var subQ0=sQuery(id+"F0.wireOp",EDGE,"E21.filletArc");var subQ1=sQuery(id+"F0.wireOp",EDGE,"E7");var subQ2=sQuery(id+"F0.wireOp",EDGE,"E6");var subQ3=sQuery(id+"F0.wireOp",EDGE,"E5");var subQ4=sQuery(id+"F0.wireOp",EDGE,"E4");var subQ5=sQuery(id+"F0.wireOp",EDGE,"E22.filletArc");var subQ6=sQuery(id+"F0.wireOp",EDGE,"E1.bottom");var subQ7=sQuery(id+"F0.wireOp",EDGE,"E1.right");var subQ8=sQuery(id+"F0.wireOp",EDGE,"E1.top");var subQ9=sQuery(id+"F0.wireOp",EDGE,"E1.left");var subQ10=sQuery(id+"F0.wireOp",EDGE,"E23.filletArc");var subQ11=sQuery(id+"F0.wireOp",EDGE,"E24.filletArc");Q0=makeQuery(id+"F2.boolean.opBoolean","SPLIT",FACE,{"disambiguationData":[TD([makeQuery(id+"F1.opExtrude","SWEPT_FACE",FACE,{"disambiguationData":[OSD([subQ6])]})])],"derivedFrom":makeQuery(id+"F1.opExtrude","CAP_FACE",FACE,{"disambiguationData":[OSD([subQ6,subQ8,subQ9,subQ7,subQ4,subQ3,subQ2,subQ1,subQ0,subQ5,subQ10,subQ11])],"isStart":true})});}
            var sketch = newSketch(context, id + "F16", { "sketchPlane" : qUnion([Q0])});
            skLineSegment(sketch, "E79.0", {"start": v(-64.25, 74.25) * mm, "end": v(64.25, 74.25) * mm});
            skArc(sketch, "E80.0", {"start": v(54.26, 47.88) * mm, "mid": v(0, 60) * mm, "end": v(-54.26, 47.88) * mm});
            skArc(sketch, "E81.0", {"start": v(-64.25, 74.25) * mm, "mid": v(-71.32, 71.32) * mm, "end": v(-74.25, 64.25) * mm});
            skLineSegment(sketch, "E82.0", {"start": v(-74.25, -64.25) * mm, "end": v(-74.25, 64.25) * mm});
            skCircle(sketch, "E83.0", {"center": v(-60, 60) * mm, "radius": 4 * mm});
            skCircle(sketch, "E84.0", {"center": v(60, 60) * mm, "radius": 4 * mm});
            skPoint(sketch, "E85.0", {"position": v(58.44, 44.2) * mm});
            skArc(sketch, "E86.0", {"start": v(60, 38.83) * mm, "mid": v(58.44, 44.2) * mm, "end": v(54.26, 47.88) * mm});
            skLineSegment(sketch, "E87.0", {"start": v(60, 38.83) * mm, "end": v(60, -38.83) * mm});
            skLineSegment(sketch, "E88.0", {"start": v(-60, 38.83) * mm, "end": v(-60, -38.83) * mm});
            skArc(sketch, "E89.0", {"start": v(-54.26, 47.88) * mm, "mid": v(-58.44, 44.2) * mm, "end": v(-60, 38.83) * mm});
            skArc(sketch, "E90.0", {"start": v(-60, -38.83) * mm, "mid": v(-58.44, -44.2) * mm, "end": v(-54.26, -47.88) * mm});
            skArc(sketch, "E91.0", {"start": v(-54.26, -47.88) * mm, "mid": v(0, -60) * mm, "end": v(54.26, -47.88) * mm});
            skArc(sketch, "E92.0", {"start": v(54.26, -47.88) * mm, "mid": v(58.44, -44.2) * mm, "end": v(60, -38.83) * mm});
            skLineSegment(sketch, "E93.0.0", {"start": v(60, -38.83) * mm, "end": v(60, 38.83) * mm});
            skLineSegment(sketch, "E94.0", {"start": v(-64.25, -74.25) * mm, "end": v(64.25, -74.25) * mm});
            skArc(sketch, "E95.0", {"start": v(64.25, -74.25) * mm, "mid": v(71.32, -71.32) * mm, "end": v(74.25, -64.25) * mm});
            skArc(sketch, "E96.0", {"start": v(-74.25, -64.25) * mm, "mid": v(-71.32, -71.32) * mm, "end": v(-64.25, -74.25) * mm});
            skLineSegment(sketch, "E97.0", {"start": v(74.25, -64.25) * mm, "end": v(74.25, 64.25) * mm});
            skArc(sketch, "E98.0", {"start": v(74.25, 64.25) * mm, "mid": v(71.32, 71.32) * mm, "end": v(64.25, 74.25) * mm});
            skCircle(sketch, "E99.0", {"center": v(-60, -60) * mm, "radius": 4 * mm});
            skCircle(sketch, "E100.0", {"center": v(60, -60) * mm, "radius": 4 * mm});
            skLineSegment(sketch, "E101", {"start": v(0, 74.25) * mm, "end": v(0, 104.25) * mm, "construction": true});
            skLineSegment(sketch, "E102", {"start": v(-35, 74.25) * mm, "end": v(-15.72, 92.25) * mm});
            skLineSegment(sketch, "E103", {"start": v(14.28, 93.52) * mm, "end": v(33.55, 74.25) * mm});
            skLineSegment(sketch, "E104", {"start": v(14.28, 93.52) * mm, "end": v(14.28, 104.25) * mm});
            skLineSegment(sketch, "E105", {"start": v(-15.72, 104.25) * mm, "end": v(-15.72, 92.25) * mm});
            skArc(sketch, "E106", {"start": v(14.28, 104.25) * mm, "mid": v(-0.72, 119.25) * mm, "end": v(-15.72, 104.25) * mm});
            skCircle(sketch, "E107", {"center": v(0, 104.25) * mm, "radius": 6 * mm});
            skLineSegment(sketch, "E108", {"start": v(-74.25, 0) * mm, "end": v(74.25, 0) * mm, "construction": true});
            skLineSegment(sketch, "E109.MirrorCS", {"start": v(14.28, -93.52) * mm, "end": v(33.55, -74.25) * mm});
            skLineSegment(sketch, "E110.MirrorCS", {"start": v(14.28, -93.52) * mm, "end": v(14.28, -104.25) * mm});
            skLineSegment(sketch, "E111.MirrorCS", {"start": v(-15.72, -104.25) * mm, "end": v(-15.72, -92.25) * mm});
            skLineSegment(sketch, "E112.MirrorCS", {"start": v(-35, -74.25) * mm, "end": v(-15.72, -92.25) * mm});
            skCircle(sketch, "E113.MirrorC", {"center": v(0, -104.25) * mm, "radius": 6 * mm});
            skArc(sketch, "E114.MirrorCS", {"start": v(14.28, -104.25) * mm, "mid": v(-0.72, -119.25) * mm, "end": v(-15.72, -104.25) * mm});
            skSolve(sketch);
        }
        {
            var Q0;
            {var subQ1=sQuery(id+"F16.wireOp",EDGE,"E102");Q0=makeQuery(id+"F16.imprint","IMPRINT",FACE,{"disambiguationData":[TD([[makeQuery(id+"F16.imprint","IMPRINT",EDGE,{"derivedFrom":subQ1}),-1.0]])]});}
            var Q1;
            {var subQ6=sQuery(id+"F16.wireOp",EDGE,"E81.0");Q1=makeQuery(id+"F16.imprint","IMPRINT",FACE,{"disambiguationData":[TD([[makeQuery(id+"F16.imprint","IMPRINT",EDGE,{"derivedFrom":subQ6}),1.0]])]});}
            var Q2;
            {var subQ0=sQuery(id+"F16.wireOp",EDGE,"E109.MirrorCS");Q2=makeQuery(id+"F16.imprint","IMPRINT",FACE,{"disambiguationData":[TD([[makeQuery(id+"F16.imprint","IMPRINT",EDGE,{"derivedFrom":subQ0}),1.0]])]});}
            var Q3;
            Q3=makeQuery(id+"F2.opExtrude","CAP_FACE",FACE,{"disambiguationData":[OSD([sQuery(id+"F0.wireOp",EDGE,"E12"),sQuery(id+"F0.wireOp",EDGE,"E13"),sQuery(id+"F0.wireOp",EDGE,"E14"),sQuery(id+"F0.wireOp",EDGE,"E15"),sQuery(id+"F0.wireOp",EDGE,"E17.filletArc"),sQuery(id+"F0.wireOp",EDGE,"E18.filletArc"),sQuery(id+"F0.wireOp",EDGE,"E19.filletArc"),sQuery(id+"F0.wireOp",EDGE,"E20.filletArc"),sQuery(id+"F0.wireOp",EDGE,"E25.0"),sQuery(id+"F0.wireOp",EDGE,"E25.1"),sQuery(id+"F0.wireOp",EDGE,"E25.2"),sQuery(id+"F0.wireOp",EDGE,"E25.3"),sQuery(id+"F0.wireOp",EDGE,"E25.4"),sQuery(id+"F0.wireOp",EDGE,"E25.5"),sQuery(id+"F0.wireOp",EDGE,"E25.6"),sQuery(id+"F0.wireOp",EDGE,"E25.7")])],"isStart":false});
            extrude(context, id + "F17", {"entities" : qUnion([Q0, Q1, Q2]), "endBound" : BoundingType.UP_TO_SURFACE, "endBoundEntityFace" : qUnion([Q3]), "depth" : 25 * mm});
        }
    });
